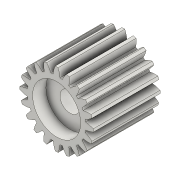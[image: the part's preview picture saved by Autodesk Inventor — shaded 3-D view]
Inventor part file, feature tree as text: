
AUTODESK INVENTOR PART (.ipt)
format: ipt  version: 2020.3 (Build 243373010, 373A)  size: 242,688 bytes
history: native  units: mm (DEFAULTED — no unit token found)
features: extrude x4, sketch x4, plane x3, other x3
ambient origin geometry x8: Origin, YZ Plane, XZ Plane, XY Plane, X Axis, Y Axis, Z Axis, Center Point
bodies: Solid1 (feature_tree)
feature tree (14):
  extrude  "Extrusion1"  Depth=10.0mm TaperAngle=0.0deg
  plane  "Work Plane2"
  plane  "Work Plane8"
  plane  "Work Plane9"
  other  "Spur Gear"
  sketch  "Sketch6"  dims[d16=15.0mm d17=0.0mm d34=1.570796mm]
  extrude  "Extrusion3"  Depth=10.0mm TaperAngle=0.0deg
  extrude  "Extrusion4"  Depth=1.570796mm TaperAngle=0.0deg
  extrude  "Extrusion5"  TaperAngle=0.0deg  [1 undecoded]
  sketch  "Sketch1"  dims[d0=11.0mm d1=10.0mm d2=0.0mm]
  sketch  "Sketch2"  dims[d3=10.0mm d4=10.0mm d5=0.0mm]
  other  "Srf1"
  sketch  "Sketch7"  dims[d39=0.0mm d41=0.0mm d43=15.0mm d46=15.0mm d47=0.0mm d48=0.0mm d52=7.2mm d53=3.0mm d54=2.0mm d55=0.0mm d56=0.0mm d57=0.0mm d58=7.2mm d59=2.0mm d60=0.0mm]
  other  "Pitch Diameter"
note: 1 required parameter value undecoded (feature->parameter linkage not recoverable at this tier; creation-order binding heuristic only, values carry confidence <= 0.55)
